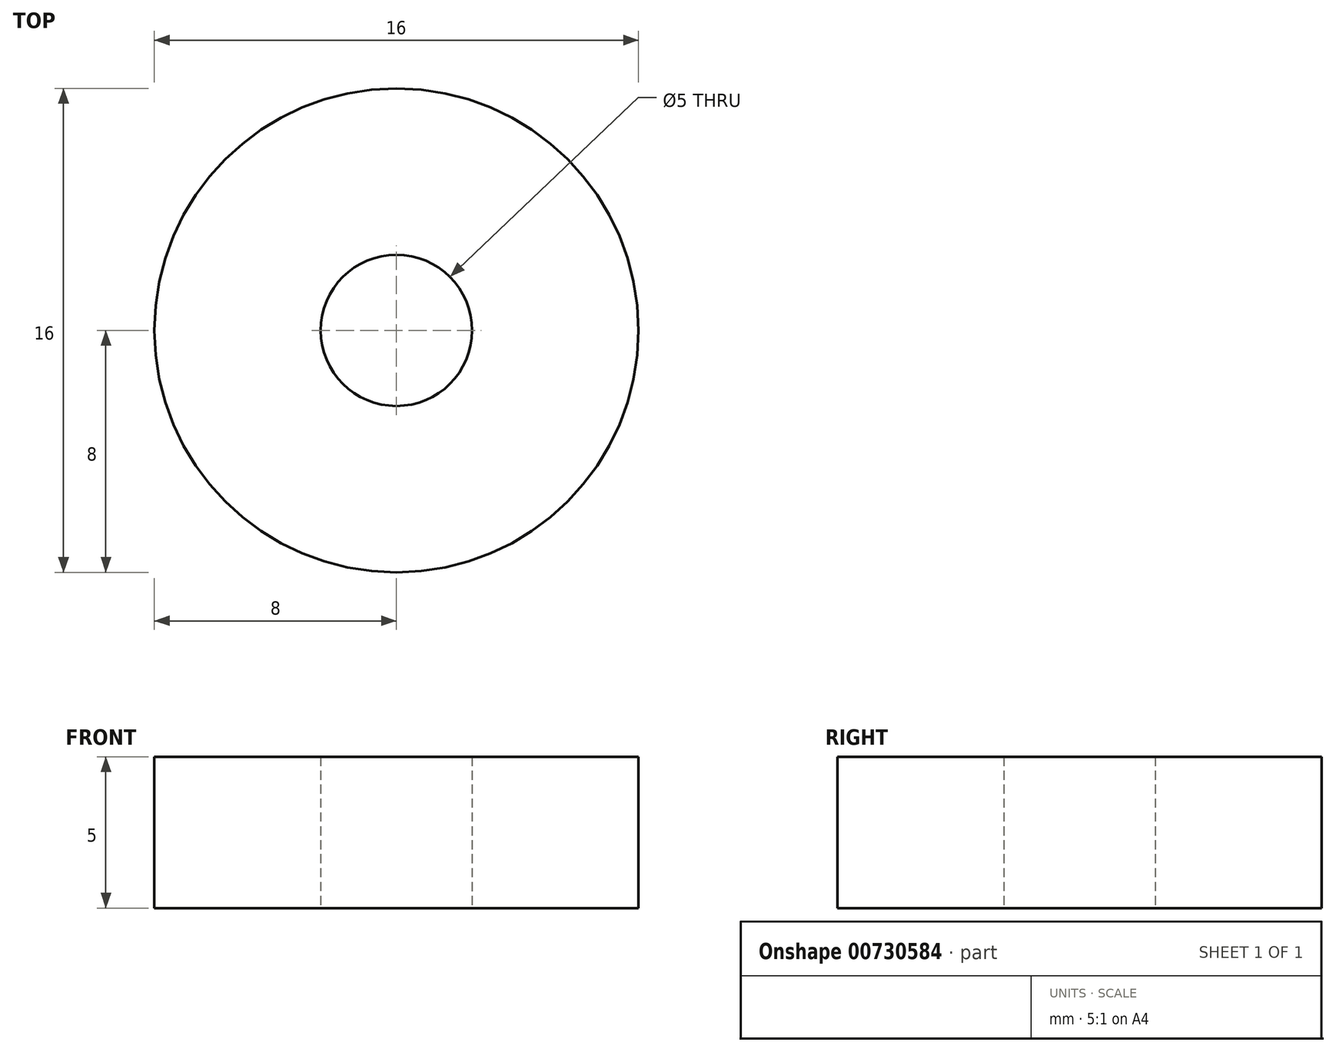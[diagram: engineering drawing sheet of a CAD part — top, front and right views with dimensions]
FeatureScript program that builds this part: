
annotation { "Feature Type Name" : "Feature", "Feature Type Description" : "" }
export const myFeature = defineFeature(function(context is Context, id is Id, definition is map)
    precondition{}
    {
        {
            var Q0;
            Q0=qCreatedBy(makeId("Top.planeOp"),FACE);
            var sketch = newSketch(context, id + "F0", { "sketchPlane" : qUnion([Q0])});
            skCircle(sketch, "E0", {"center": v(0, 0) * mm, "radius": 8 * mm});
            skCircle(sketch, "E1", {"center": v(0, 0) * mm, "radius": 2.5 * mm});
            skSolve(sketch);
        }
        {
            var Q0;
            Q0 = qSketchRegion(id + "F0", true);
            extrude(context, id + "F1", {"entities" : qUnion([Q0]), "depth" : 5 * mm, "offsetDistance" : 25 * mm});
        }
    });
